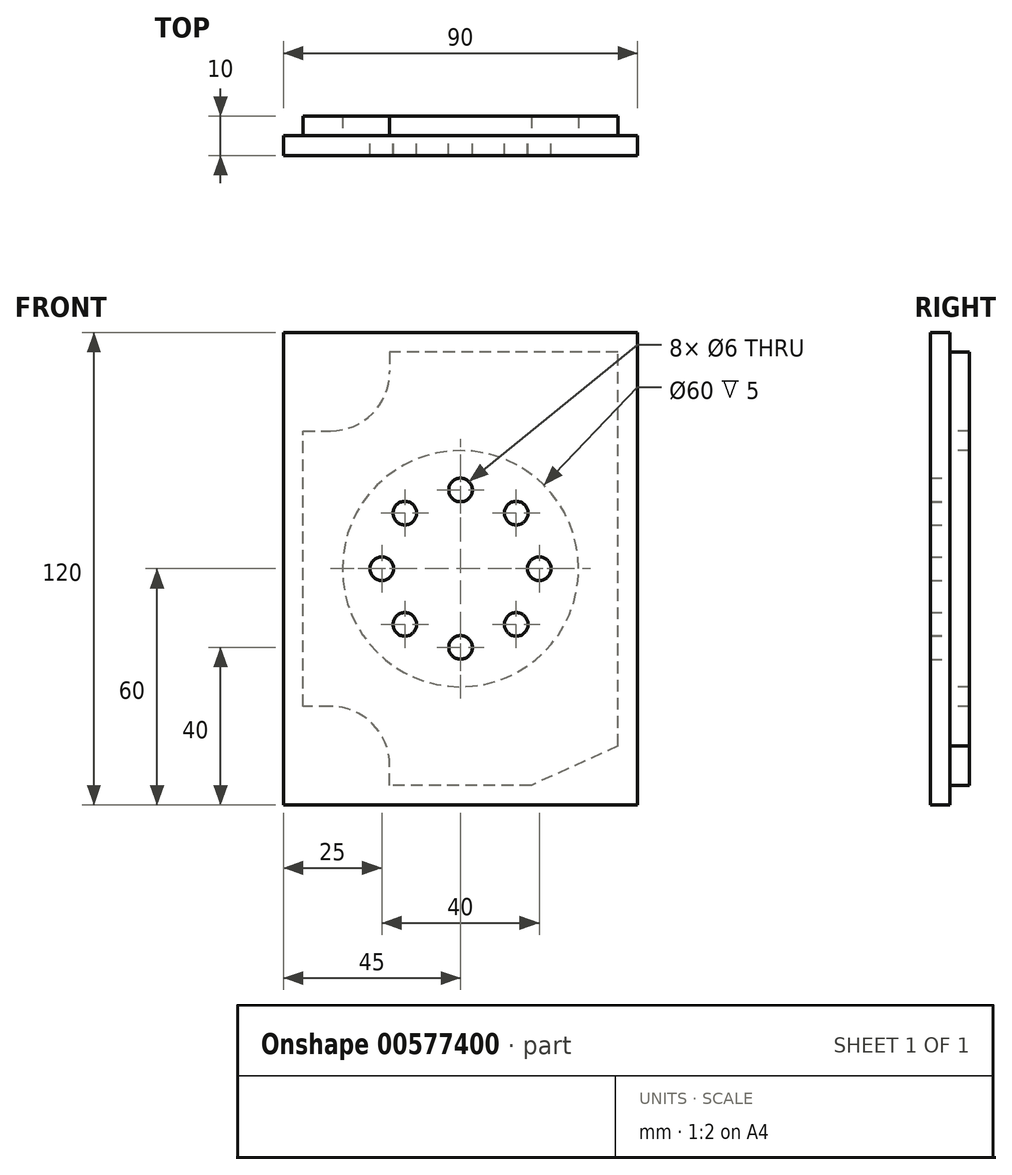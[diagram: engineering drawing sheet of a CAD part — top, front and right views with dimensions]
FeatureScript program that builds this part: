
annotation { "Feature Type Name" : "Feature", "Feature Type Description" : "" }
export const myFeature = defineFeature(function(context is Context, id is Id, definition is map)
    precondition{}
    {
        {
            var Q0;
            Q0=qCreatedBy(makeId("Front.planeOp"),FACE);
            var sketch = newSketch(context, id + "F0", { "sketchPlane" : qUnion([Q0])});
            skLineSegment(sketch, "E0", {"start": v(0, 0) * mm, "end": v(45, 0) * mm, "construction": true});
            skLineSegment(sketch, "E1", {"start": v(45, 0) * mm, "end": v(45, -60) * mm});
            skLineSegment(sketch, "E2", {"start": v(45, -60) * mm, "end": v(0, -60) * mm});
            skLineSegment(sketch, "E3", {"start": v(0, -60) * mm, "end": v(0, 0) * mm, "construction": true});
            skLineSegment(sketch, "E4.MirrorCS", {"start": v(-45, -60) * mm, "end": v(0, -60) * mm});
            skLineSegment(sketch, "E5.MirrorCS", {"start": v(-45, 0) * mm, "end": v(-45, -60) * mm});
            skLineSegment(sketch, "E6.MirrorCS", {"start": v(45, 60) * mm, "end": v(0, 60) * mm});
            skLineSegment(sketch, "E7.MirrorCS", {"start": v(45, 0) * mm, "end": v(45, 60) * mm});
            skLineSegment(sketch, "E8.MirrorCS", {"start": v(-45, 0) * mm, "end": v(-45, 60) * mm});
            skLineSegment(sketch, "E9.MirrorCS", {"start": v(-45, 60) * mm, "end": v(0, 60) * mm});
            skSolve(sketch);
        }
        {
            var Q0;
            Q0=makeQuery(id+"F0.imprint","IMPRINT",FACE,{"disambiguationData":[TD([[makeQuery(id+"F0.imprint","IMPRINT",EDGE,{"derivedFrom":sQuery(id+"F0.wireOp",EDGE,"E1")}),-1.0]])]});
            extrude(context, id + "F1", {"entities" : qUnion([Q0]), "depth" : 5 * mm, "offsetDistance" : 25 * mm});
        }
        {
            var Q0;
            Q0=makeQuery(id+"F1.opExtrude","CAP_FACE",FACE,{"disambiguationData":[OSD([sQuery(id+"F0.wireOp",EDGE,"E1"),sQuery(id+"F0.wireOp",EDGE,"E2"),sQuery(id+"F0.wireOp",EDGE,"E4.MirrorCS"),sQuery(id+"F0.wireOp",EDGE,"E5.MirrorCS"),sQuery(id+"F0.wireOp",EDGE,"E6.MirrorCS"),sQuery(id+"F0.wireOp",EDGE,"E7.MirrorCS"),sQuery(id+"F0.wireOp",EDGE,"E8.MirrorCS"),sQuery(id+"F0.wireOp",EDGE,"E9.MirrorCS")])],"isStart":true});
            var sketch = newSketch(context, id + "F2", { "sketchPlane" : qUnion([Q0])});
            skLineSegment(sketch, "E10", {"start": v(-40, -45) * mm, "end": v(-40, 55) * mm});
            skLineSegment(sketch, "E11", {"start": v(-40, 55) * mm, "end": v(18, 55) * mm});
            skLineSegment(sketch, "E12", {"start": v(18, 55) * mm, "end": v(18, 50) * mm});
            skLineSegment(sketch, "E13", {"start": v(-40, -45) * mm, "end": v(-18, -55) * mm});
            skLineSegment(sketch, "E14", {"start": v(-18, -55) * mm, "end": v(18, -55) * mm});
            skLineSegment(sketch, "E15", {"start": v(18, -55) * mm, "end": v(18, -50) * mm});
            skArc(sketch, "E16", {"start": v(33, -35) * mm, "mid": v(22.4, -39.4) * mm, "end": v(18, -50) * mm});
            skArc(sketch, "E17", {"start": v(18, 50) * mm, "mid": v(22.4, 39.4) * mm, "end": v(33, 35) * mm});
            skLineSegment(sketch, "E18", {"start": v(33, -35) * mm, "end": v(40, -35) * mm});
            skLineSegment(sketch, "E19", {"start": v(40, -35) * mm, "end": v(40, 35) * mm});
            skLineSegment(sketch, "E20", {"start": v(40, 35) * mm, "end": v(33, 35) * mm});
            skCircle(sketch, "E21", {"center": v(0, 0) * mm, "radius": 30 * mm});
            skSolve(sketch);
        }
        {
            var Q0;
            Q0=makeQuery(id+"F2.imprint","IMPRINT",FACE,{"disambiguationData":[TD([[makeQuery(id+"F2.imprint","IMPRINT",EDGE,{"derivedFrom":sQuery(id+"F2.wireOp",EDGE,"E10")}),-1.0]])]});
            extrude(context, id + "F3", {"entities" : qUnion([Q0]), "operationType" : NewBodyOperationType.ADD, "depth" : 5 * mm, "offsetDistance" : 25 * mm});
        }
        {
            var Q0;
            Q0=makeQuery(id+"F3.boolean.opBoolean","SPLIT",FACE,{"disambiguationData":[TD([makeQuery(id+"F3.opExtrude","SWEPT_FACE",FACE,{"disambiguationData":[OSD([sQuery(id+"F2.wireOp",EDGE,"E21")])]})])],"derivedFrom":makeQuery(id+"F1.opExtrude","CAP_FACE",FACE,{"disambiguationData":[OSD([sQuery(id+"F0.wireOp",EDGE,"E1"),sQuery(id+"F0.wireOp",EDGE,"E2"),sQuery(id+"F0.wireOp",EDGE,"E4.MirrorCS"),sQuery(id+"F0.wireOp",EDGE,"E5.MirrorCS"),sQuery(id+"F0.wireOp",EDGE,"E6.MirrorCS"),sQuery(id+"F0.wireOp",EDGE,"E7.MirrorCS"),sQuery(id+"F0.wireOp",EDGE,"E8.MirrorCS"),sQuery(id+"F0.wireOp",EDGE,"E9.MirrorCS")])],"isStart":true})});
            var sketch = newSketch(context, id + "F4", { "sketchPlane" : qUnion([Q0])});
            skCircle(sketch, "E22", {"center": v(0, 0) * mm, "radius": 20 * mm, "construction": true});
            skCircle(sketch, "E23", {"center": v(-20, 0) * mm, "radius": 3 * mm});
            skCircle(sketch, "E24", {"center": v(0, 20) * mm, "radius": 3 * mm});
            skCircle(sketch, "E25", {"center": v(20, 0) * mm, "radius": 3 * mm});
            skCircle(sketch, "E26", {"center": v(0, -20) * mm, "radius": 3 * mm});
            skCircle(sketch, "E27", {"center": v(-14.14, 14.14) * mm, "radius": 3 * mm});
            skCircle(sketch, "E28", {"center": v(-14.14, -14.14) * mm, "radius": 3 * mm});
            skCircle(sketch, "E29", {"center": v(14.14, 14.14) * mm, "radius": 3 * mm});
            skCircle(sketch, "E30", {"center": v(14.14, -14.14) * mm, "radius": 3 * mm});
            skSolve(sketch);
        }
        {
            var Q0;
            Q0=makeQuery(id+"F4.imprint","IMPRINT",FACE,{"disambiguationData":[TD([[makeQuery(id+"F4.imprint","IMPRINT",EDGE,{"derivedFrom":sQuery(id+"F4.wireOp",EDGE,"E28")}),1.0]])]});
            var Q1;
            Q1=makeQuery(id+"F4.imprint","IMPRINT",FACE,{"disambiguationData":[TD([[makeQuery(id+"F4.imprint","IMPRINT",EDGE,{"derivedFrom":sQuery(id+"F4.wireOp",EDGE,"E23")}),1.0]])]});
            var Q2;
            Q2=makeQuery(id+"F4.imprint","IMPRINT",FACE,{"disambiguationData":[TD([[makeQuery(id+"F4.imprint","IMPRINT",EDGE,{"derivedFrom":sQuery(id+"F4.wireOp",EDGE,"E27")}),1.0]])]});
            var Q3;
            Q3=makeQuery(id+"F4.imprint","IMPRINT",FACE,{"disambiguationData":[TD([[makeQuery(id+"F4.imprint","IMPRINT",EDGE,{"derivedFrom":sQuery(id+"F4.wireOp",EDGE,"E24")}),1.0]])]});
            var Q4;
            Q4=makeQuery(id+"F4.imprint","IMPRINT",FACE,{"disambiguationData":[TD([[makeQuery(id+"F4.imprint","IMPRINT",EDGE,{"derivedFrom":sQuery(id+"F4.wireOp",EDGE,"E29")}),1.0]])]});
            var Q5;
            Q5=makeQuery(id+"F4.imprint","IMPRINT",FACE,{"disambiguationData":[TD([[makeQuery(id+"F4.imprint","IMPRINT",EDGE,{"derivedFrom":sQuery(id+"F4.wireOp",EDGE,"E25")}),1.0]])]});
            var Q6;
            Q6=makeQuery(id+"F4.imprint","IMPRINT",FACE,{"disambiguationData":[TD([[makeQuery(id+"F4.imprint","IMPRINT",EDGE,{"derivedFrom":sQuery(id+"F4.wireOp",EDGE,"E30")}),1.0]])]});
            var Q7;
            Q7=makeQuery(id+"F4.imprint","IMPRINT",FACE,{"disambiguationData":[TD([[makeQuery(id+"F4.imprint","IMPRINT",EDGE,{"derivedFrom":sQuery(id+"F4.wireOp",EDGE,"E26")}),1.0]])]});
            extrude(context, id + "F5", {"entities" : qUnion([Q0, Q1, Q2, Q3, Q4, Q5, Q6, Q7]), "operationType" : NewBodyOperationType.REMOVE, "oppositeDirection" : true, "depth" : 5 * mm, "offsetDistance" : 25 * mm});
        }
    });
